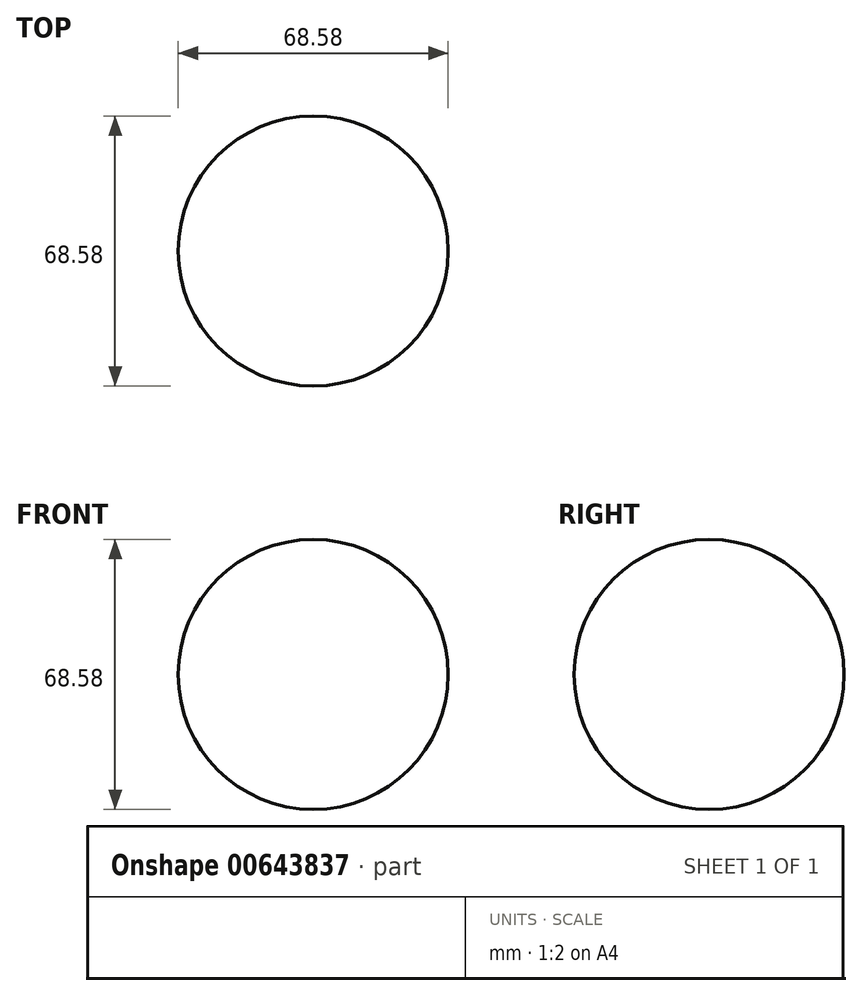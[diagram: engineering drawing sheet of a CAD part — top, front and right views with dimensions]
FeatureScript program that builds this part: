
annotation { "Feature Type Name" : "Feature", "Feature Type Description" : "" }
export const myFeature = defineFeature(function(context is Context, id is Id, definition is map)
    precondition{}
    {
        {
            var Q0;
            Q0=qCreatedBy(makeId("Front.planeOp"),FACE);
            var sketch = newSketch(context, id + "F0", { "sketchPlane" : qUnion([Q0])});
            skCircle(sketch, "E0", {"center": v(0, 0) * mm, "radius": 34.29 * mm});
            skLineSegment(sketch, "E1", {"start": v(-45.63, 0) * mm, "end": v(45.64, 0) * mm});
            skSolve(sketch);
        }
        {
            var Q0;
            {var subQ0=sQuery(id+"F0.wireOp",EDGE,"E1");var subQ1=sQuery(id+"F0.wireOp",EDGE,"E0");var subQ2=makeQuery(id+"F0.imprint","INTERSECT",VERTEX,{"disambiguationData":[OD(0.0)],"derivedFrom":[subQ1,subQ0]});Q0=makeQuery(id+"F0.imprint","IMPRINT",FACE,{"disambiguationData":[TD([[makeQuery(id+"F0.imprint","IMPRINT",EDGE,{"disambiguationData":[TD([[subQ2,1.0]])],"derivedFrom":subQ1}),1.0]])]});}
            var Q1;
            Q1=sQuery(id+"F0.wireOp",EDGE,"E1");
            revolve(context, id + "F1", {"entities" : qUnion([Q0]), "axis" : qUnion([Q1]), "revolveType" : RevolveType.FULL});
        }
    });
